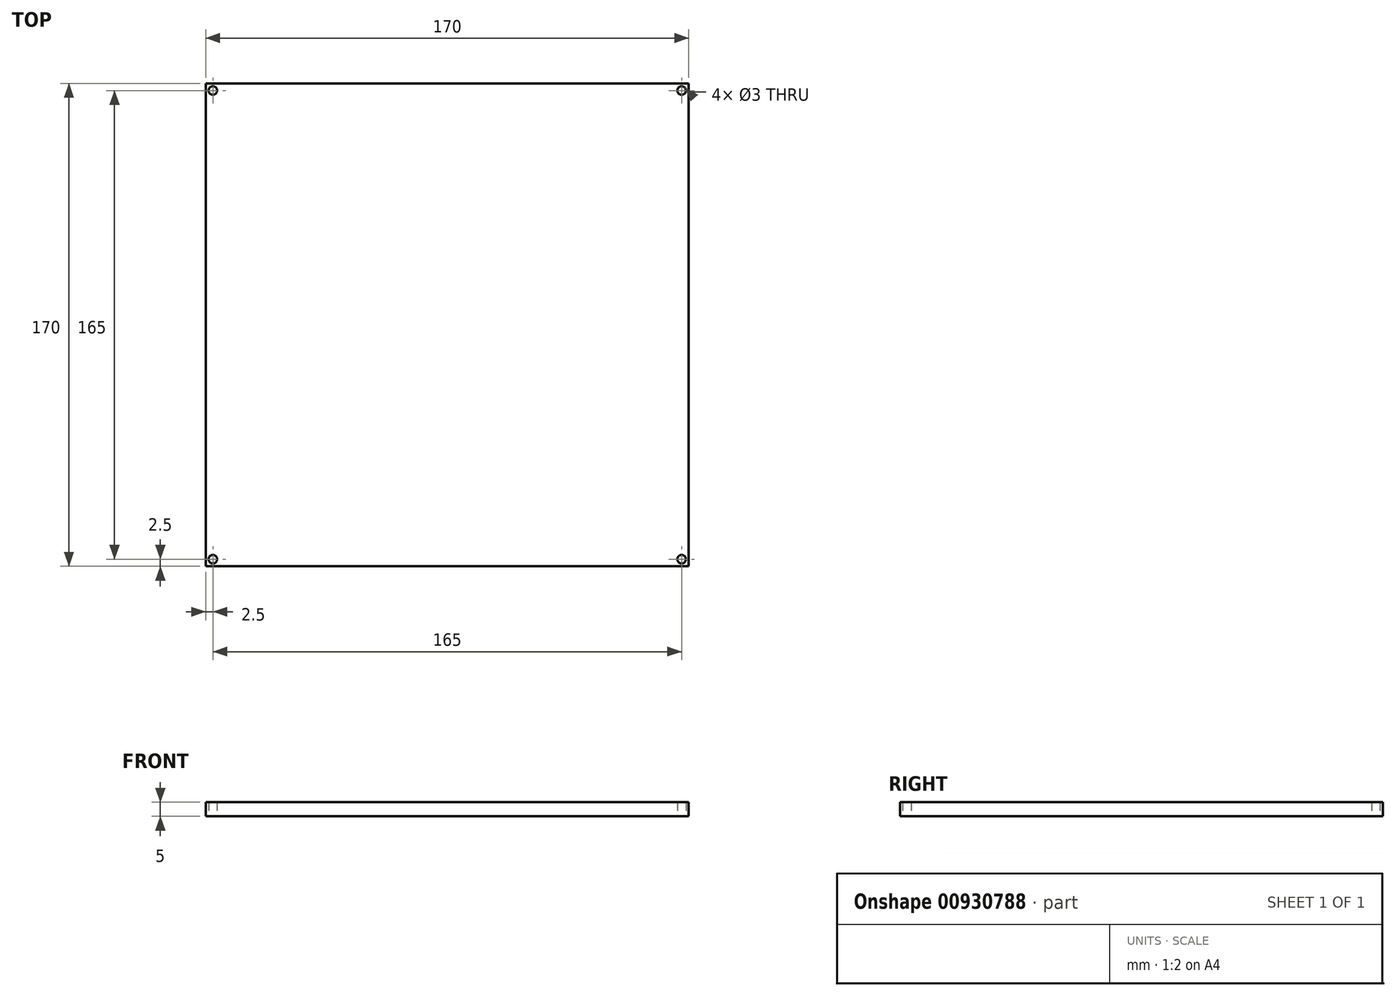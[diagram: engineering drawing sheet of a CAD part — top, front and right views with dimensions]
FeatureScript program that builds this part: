
annotation { "Feature Type Name" : "Feature", "Feature Type Description" : "" }
export const myFeature = defineFeature(function(context is Context, id is Id, definition is map)
    precondition{}
    {
        {
            var Q0;
            Q0=qCreatedBy(makeId("Top.planeOp"),FACE);
            var sketch = newSketch(context, id + "F0", { "sketchPlane" : qUnion([Q0])});
            skLineSegment(sketch, "E0.bottom", {"start": v(85, -85) * mm, "end": v(-85, -85) * mm});
            skLineSegment(sketch, "E0.top", {"start": v(85, 85) * mm, "end": v(-85, 85) * mm});
            skLineSegment(sketch, "E0.left", {"start": v(85, -85) * mm, "end": v(85, 85) * mm});
            skLineSegment(sketch, "E0.right", {"start": v(-85, -85) * mm, "end": v(-85, 85) * mm});
            skPoint(sketch, "E0.middle", {"position": v(0, 0) * mm});
            skLineSegment(sketch, "E1.0", {"start": v(80, 80) * mm, "end": v(-80, 80) * mm});
            skLineSegment(sketch, "E1.1", {"start": v(80, -80) * mm, "end": v(80, 80) * mm});
            skLineSegment(sketch, "E1.2", {"start": v(80, -80) * mm, "end": v(-80, -80) * mm});
            skLineSegment(sketch, "E1.3", {"start": v(-80, -80) * mm, "end": v(-80, 80) * mm});
            skLineSegment(sketch, "E2", {"start": v(-85, 85) * mm, "end": v(-80, 80) * mm});
            skCircle(sketch, "E3", {"center": v(-82.5, 82.5) * mm, "radius": 1.5 * mm});
            skLineSegment(sketch, "E4", {"start": v(80, 80) * mm, "end": v(85, 85) * mm});
            skCircle(sketch, "E5", {"center": v(82.5, 82.5) * mm, "radius": 1.5 * mm});
            skLineSegment(sketch, "E6", {"start": v(85, -85) * mm, "end": v(80, -80) * mm});
            skCircle(sketch, "E7", {"center": v(82.5, -82.5) * mm, "radius": 1.5 * mm});
            skLineSegment(sketch, "E8", {"start": v(-85, -85) * mm, "end": v(-80, -80) * mm});
            skCircle(sketch, "E9", {"center": v(-82.5, -82.5) * mm, "radius": 1.5 * mm});
            skSolve(sketch);
        }
        {
            var Q0;
            Q0=makeQuery(id+"F0.imprint","IMPRINT",FACE,{"disambiguationData":[TD([[makeQuery(id+"F0.imprint","IMPRINT",EDGE,{"derivedFrom":sQuery(id+"F0.wireOp",EDGE,"E0.bottom")}),-1.0]])]});
            var Q1;
            {var subQ4=sQuery(id+"F0.wireOp",EDGE,"E0.right");Q1=makeQuery(id+"F0.imprint","IMPRINT",FACE,{"disambiguationData":[TD([[makeQuery(id+"F0.imprint","IMPRINT",EDGE,{"derivedFrom":subQ4}),-1.0]])]});}
            var Q2;
            {var subQ1=sQuery(id+"F0.wireOp",EDGE,"E0.left");Q2=makeQuery(id+"F0.imprint","IMPRINT",FACE,{"disambiguationData":[TD([[makeQuery(id+"F0.imprint","IMPRINT",EDGE,{"derivedFrom":subQ1}),1.0]])]});}
            var Q3;
            {var subQ1=sQuery(id+"F0.wireOp",EDGE,"E0.top");Q3=makeQuery(id+"F0.imprint","IMPRINT",FACE,{"disambiguationData":[TD([[makeQuery(id+"F0.imprint","IMPRINT",EDGE,{"derivedFrom":subQ1}),1.0]])]});}
            var Q4;
            Q4=makeQuery(id+"F0.imprint","IMPRINT",FACE,{"disambiguationData":[TD([[makeQuery(id+"F0.imprint","IMPRINT",EDGE,{"derivedFrom":sQuery(id+"F0.wireOp",EDGE,"E1.0")}),1.0]])]});
            extrude(context, id + "F1", {"entities" : qUnion([Q0, Q1, Q2, Q3, Q4]), "depth" : 5 * mm, "offsetDistance" : 25 * mm});
        }
    });
